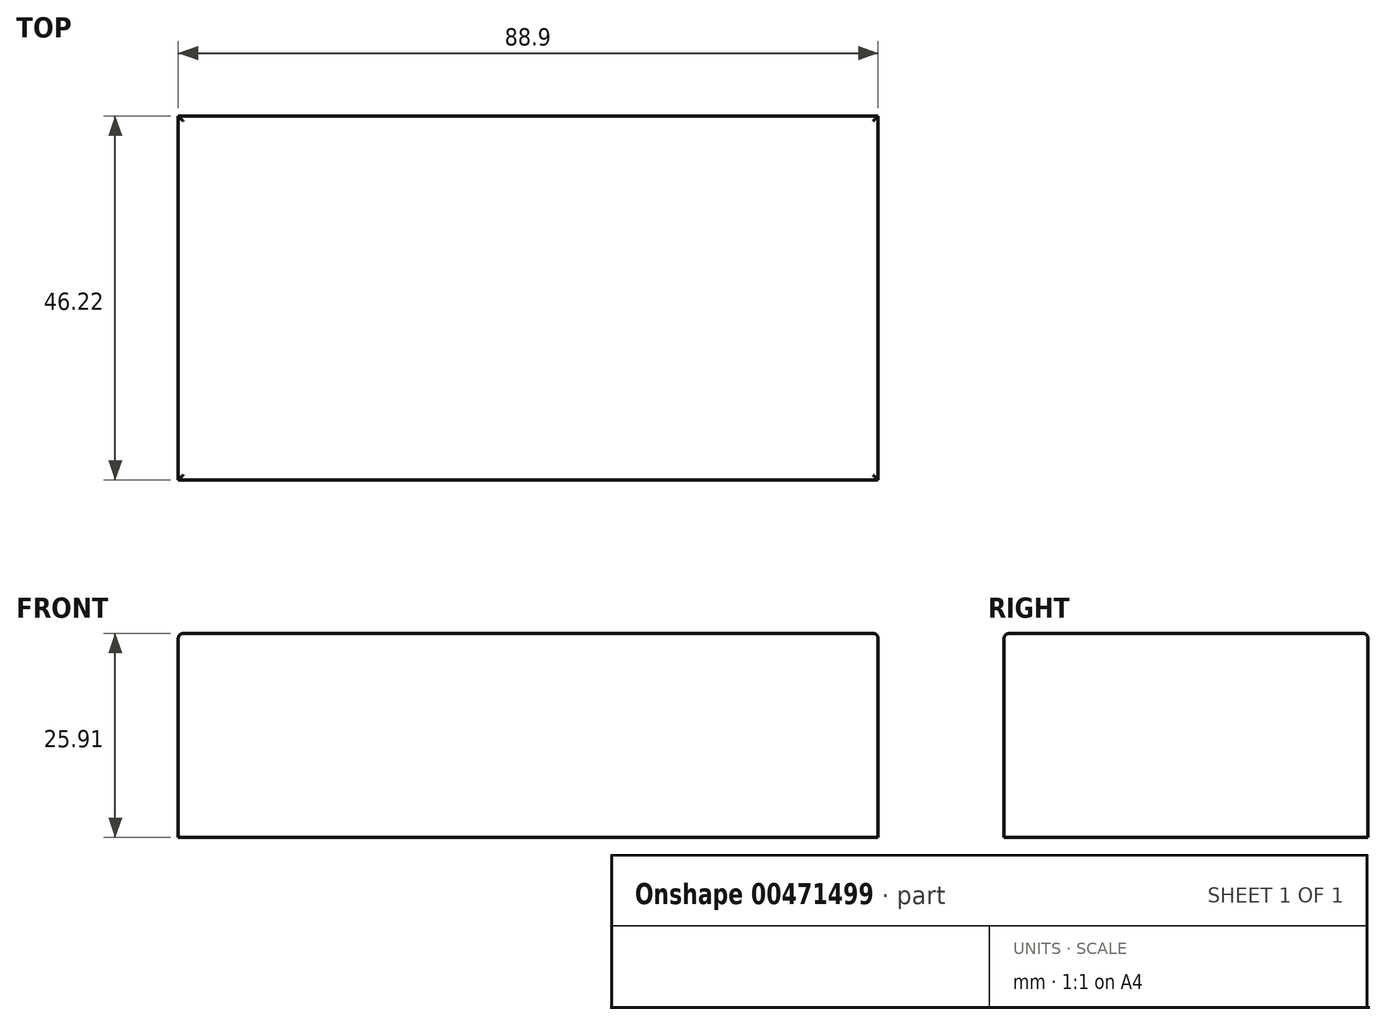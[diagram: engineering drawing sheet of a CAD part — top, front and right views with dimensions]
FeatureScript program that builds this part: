
annotation { "Feature Type Name" : "Feature", "Feature Type Description" : "" }
export const myFeature = defineFeature(function(context is Context, id is Id, definition is map)
    precondition{}
    {
        {
            var Q0;
            Q0=qCreatedBy(makeId("Top.planeOp"),FACE);
            var sketch = newSketch(context, id + "F0", { "sketchPlane" : qUnion([Q0])});
            skLineSegment(sketch, "E0.bottom", {"start": v(44.45, 23.11) * mm, "end": v(-44.45, 23.11) * mm});
            skLineSegment(sketch, "E0.top", {"start": v(44.45, -23.11) * mm, "end": v(-44.45, -23.11) * mm});
            skLineSegment(sketch, "E0.left", {"start": v(44.45, 23.11) * mm, "end": v(44.45, -23.11) * mm});
            skLineSegment(sketch, "E0.right", {"start": v(-44.45, 23.11) * mm, "end": v(-44.45, -23.11) * mm});
            skPoint(sketch, "E0.middle", {"position": v(0, 0) * mm});
            skSolve(sketch);
        }
        {
            var Q0;
            Q0=makeQuery(id+"F0.imprint","IMPRINT",FACE,{"disambiguationData":[TD([[makeQuery(id+"F0.imprint","IMPRINT",EDGE,{"derivedFrom":sQuery(id+"F0.wireOp",EDGE,"E0.bottom")}),1.0]])]});
            extrude(context, id + "F1", {"entities" : qUnion([Q0]), "depth" : 25.9 * mm});
        }
        {
            var Q0;
            Q0=makeQuery(id+"F1.opExtrude","CAP_EDGE",EDGE,{"disambiguationData":[OSD([sQuery(id+"F0.wireOp",EDGE,"E0.left")])],"isStart":false});
            var Q1;
            Q1=makeQuery(id+"F1.opExtrude","CAP_EDGE",EDGE,{"disambiguationData":[OSD([sQuery(id+"F0.wireOp",EDGE,"E0.top")])],"isStart":false});
            var Q2;
            Q2=makeQuery(id+"F1.opExtrude","CAP_EDGE",EDGE,{"disambiguationData":[OSD([sQuery(id+"F0.wireOp",EDGE,"E0.right")])],"isStart":false});
            var Q3;
            Q3=makeQuery(id+"F1.opExtrude","CAP_EDGE",EDGE,{"disambiguationData":[OSD([sQuery(id+"F0.wireOp",EDGE,"E0.bottom")])],"isStart":false});
            fillet(context, id + "F2", {"entities" : qUnion([Q0, Q1, Q2, Q3]), "radius" : 0.64 * mm, "tangentPropagation" : true, "allowEdgeOverflow" : false});
        }
    });
